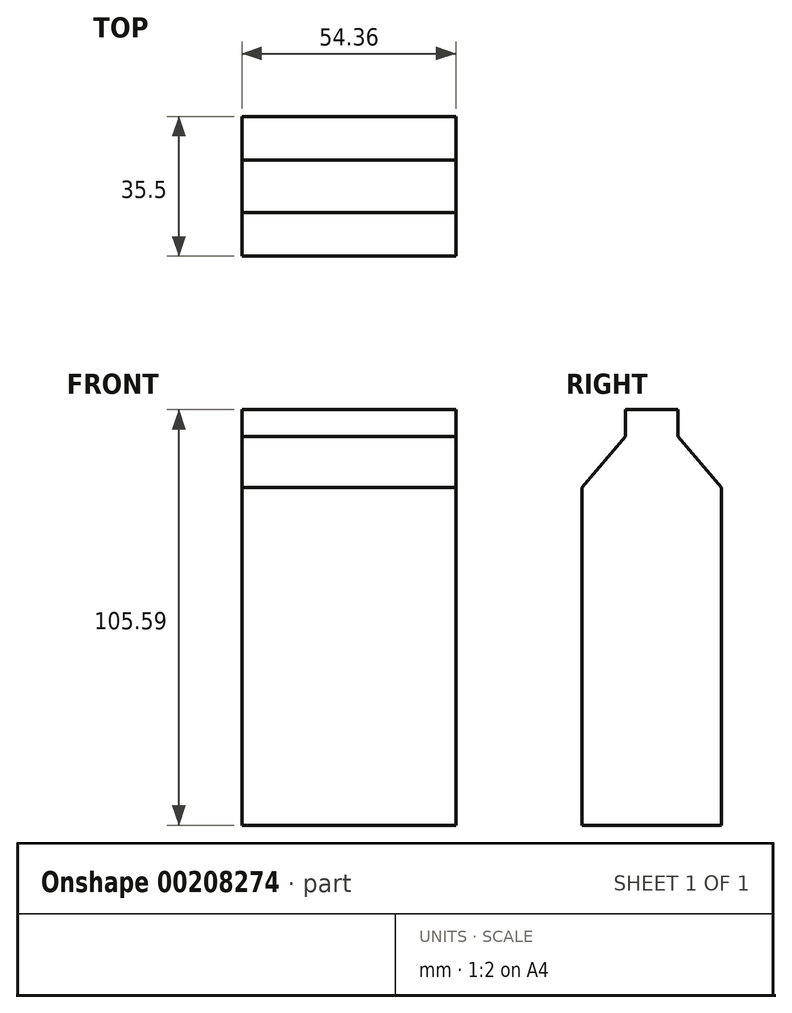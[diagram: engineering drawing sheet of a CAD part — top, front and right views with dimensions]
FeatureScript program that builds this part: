
annotation { "Feature Type Name" : "Feature", "Feature Type Description" : "" }
export const myFeature = defineFeature(function(context is Context, id is Id, definition is map)
    precondition{}
    {
        {
            var Q0;
            Q0=qCreatedBy(makeId("Right.planeOp"),FACE);
            var sketch = newSketch(context, id + "F0", { "sketchPlane" : qUnion([Q0])});
            skLineSegment(sketch, "E0.bottom", {"start": v(-17.75, 42.89) * mm, "end": v(17.75, 42.89) * mm});
            skLineSegment(sketch, "E0.top", {"start": v(-17.75, -42.89) * mm, "end": v(17.75, -42.89) * mm});
            skLineSegment(sketch, "E0.left", {"start": v(-17.75, 42.89) * mm, "end": v(-17.75, -42.89) * mm});
            skLineSegment(sketch, "E0.right", {"start": v(17.75, 42.89) * mm, "end": v(17.75, -42.89) * mm});
            skPoint(sketch, "E0.middle", {"position": v(0, 0) * mm});
            skLineSegment(sketch, "E1", {"start": v(-17.75, 42.89) * mm, "end": v(-6.7, 55.84) * mm});
            skLineSegment(sketch, "E2", {"start": v(-6.7, 55.84) * mm, "end": v(-6.7, 62.7) * mm});
            skLineSegment(sketch, "E3", {"start": v(-6.7, 62.7) * mm, "end": v(0, 62.7) * mm});
            skLineSegment(sketch, "E4.MirrorCS", {"start": v(6.7, 62.7) * mm, "end": v(0, 62.7) * mm});
            skLineSegment(sketch, "E5.MirrorCS", {"start": v(6.7, 55.84) * mm, "end": v(6.7, 62.7) * mm});
            skLineSegment(sketch, "E6.MirrorCS", {"start": v(17.75, 42.89) * mm, "end": v(6.7, 55.84) * mm});
            skSolve(sketch);
        }
        {
            var Q0;
            Q0=makeQuery(id+"F0.imprint","IMPRINT",FACE,{"disambiguationData":[TD([[makeQuery(id+"F0.imprint","IMPRINT",EDGE,{"derivedFrom":sQuery(id+"F0.wireOp",EDGE,"E0.bottom")}),-1.0]])]});
            var Q1;
            Q1=makeQuery(id+"F0.imprint","IMPRINT",FACE,{"disambiguationData":[TD([[makeQuery(id+"F0.imprint","IMPRINT",EDGE,{"derivedFrom":sQuery(id+"F0.wireOp",EDGE,"E0.bottom")}),1.0]])]});
            extrude(context, id + "F1", {"entities" : qUnion([Q0, Q1]), "endBound" : BoundingType.SYMMETRIC, "depth" : 54.36 * mm});
        }
    });
